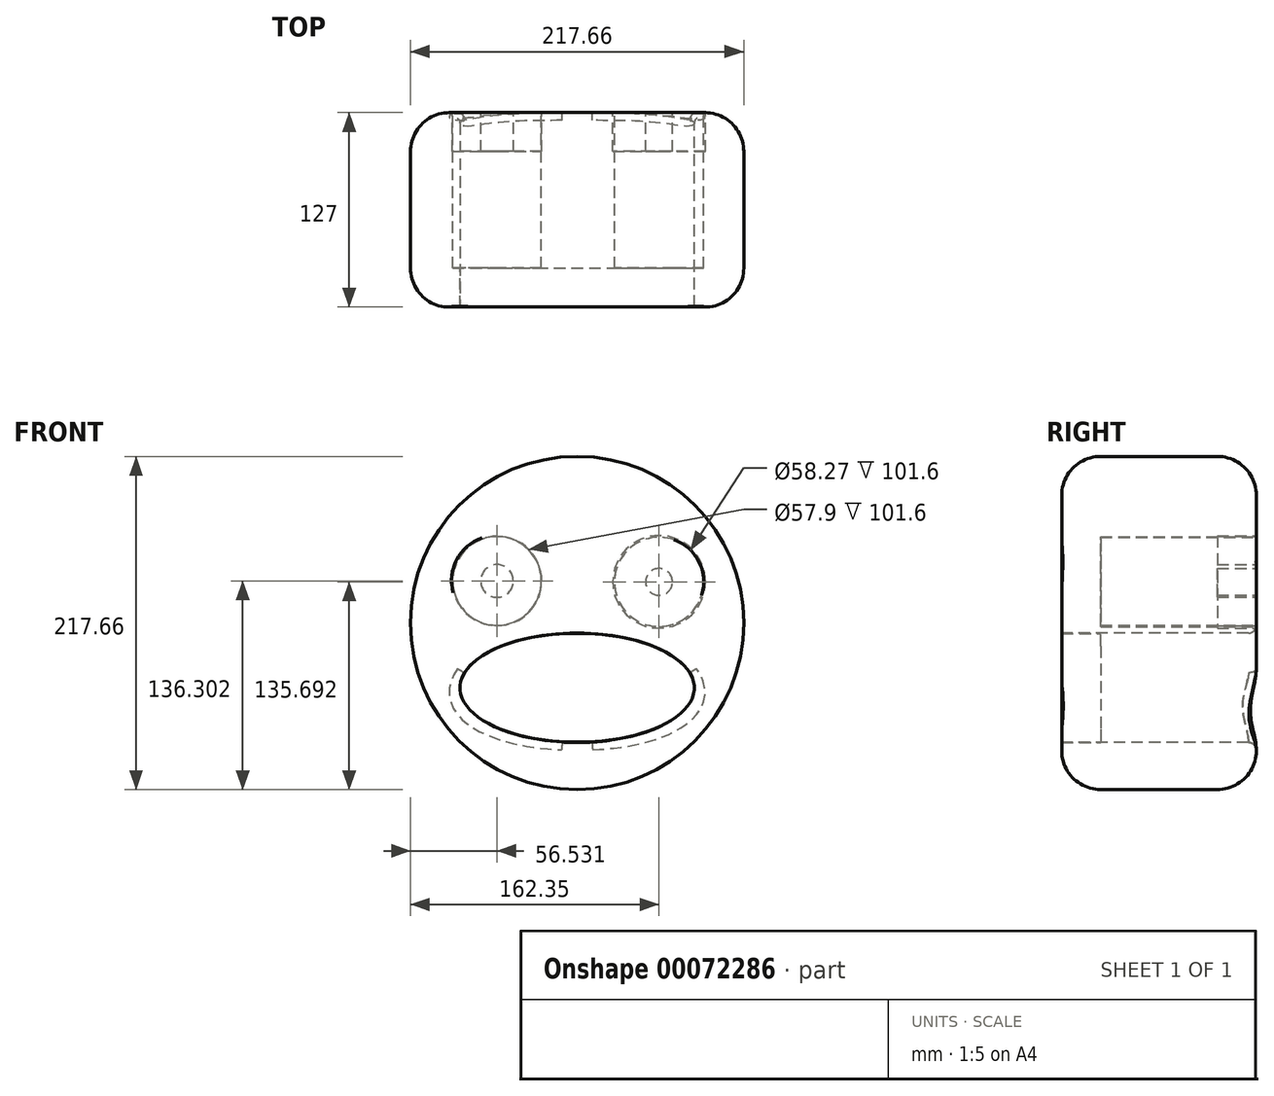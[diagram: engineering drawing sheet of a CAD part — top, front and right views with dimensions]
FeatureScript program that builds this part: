
annotation { "Feature Type Name" : "Feature", "Feature Type Description" : "" }
export const myFeature = defineFeature(function(context is Context, id is Id, definition is map)
    precondition{}
    {
        {
            var Q0;
            Q0=qCreatedBy(makeId("Front.planeOp"),FACE);
            var sketch = newSketch(context, id + "F0", { "sketchPlane" : qUnion([Q0])});
            skCircle(sketch, "E0", {"center": v(0, 0) * mm, "radius": 108.83 * mm});
            skCircle(sketch, "E1", {"center": v(-52.3, 27.47) * mm, "radius": 28.95 * mm});
            skCircle(sketch, "E2", {"center": v(53.52, 26.86) * mm, "radius": 29.14 * mm});
            skCircle(sketch, "E3", {"center": v(-52.3, 27.47) * mm, "radius": 10.65 * mm});
            skCircle(sketch, "E4", {"center": v(53.52, 26.86) * mm, "radius": 8.74 * mm});
            skEllipse(sketch, "E5", {"center": v(0, -42.33) * mm, "majorRadius": 76.51 * mm, "minorRadius": 35.71 * mm, "majorAxis": v(1, 0)});
            skSolve(sketch);
        }
        {
            var Q0;
            Q0 = qSketchRegion(id + "F0", true);
            extrude(context, id + "F1", {"entities" : qUnion([Q0]), "depth" : 127 * mm});
        }
        {
            var Q0;
            Q0=makeQuery(id+"F0.imprint","IMPRINT",FACE,{"disambiguationData":[TD([[makeQuery(id+"F0.imprint","IMPRINT",EDGE,{"derivedFrom":sQuery(id+"F0.wireOp",EDGE,"E4")}),1.0]])]});
            var Q1;
            Q1=makeQuery(id+"F0.imprint","IMPRINT",FACE,{"disambiguationData":[TD([[makeQuery(id+"F0.imprint","IMPRINT",EDGE,{"derivedFrom":sQuery(id+"F0.wireOp",EDGE,"E3")}),1.0]])]});
            extrude(context, id + "F2", {"entities" : qUnion([Q0, Q1]), "depth" : 25.4 * mm});
        }
        {
            var Q0;
            Q0=makeQuery(id+"F1.opExtrude","CAP_FACE",FACE,{"disambiguationData":[OSD([sQuery(id+"F0.wireOp",EDGE,"E0"),sQuery(id+"F0.wireOp",EDGE,"E1"),sQuery(id+"F0.wireOp",EDGE,"E2"),sQuery(id+"F0.wireOp",EDGE,"E5")])],"isStart":true});
            var sketch = newSketch(context, id + "F3", { "sketchPlane" : qUnion([Q0])});
            skCircle(sketch, "E6", {"center": v(-53.52, 26.86) * mm, "radius": 30.23 * mm});
            skCircle(sketch, "E7", {"center": v(52.3, 27.47) * mm, "radius": 29.21 * mm});
            skSolve(sketch);
        }
        {
            var Q0;
            Q0 = qSketchRegion(id + "F3", true);
            extrude(context, id + "F4", {"entities" : qUnion([Q0]), "oppositeDirection" : true, "depth" : 25.4 * mm});
        }
        {
            var Q0;
            Q0=makeQuery(id+"F1.opExtrude","CAP_FACE",FACE,{"disambiguationData":[OSD([sQuery(id+"F0.wireOp",EDGE,"E0"),sQuery(id+"F0.wireOp",EDGE,"E1"),sQuery(id+"F0.wireOp",EDGE,"E2"),sQuery(id+"F0.wireOp",EDGE,"E5")])],"isStart":false});
            var sketch = newSketch(context, id + "F5", { "sketchPlane" : qUnion([Q0])});
            skEllipse(sketch, "E8", {"center": v(0, -42.33) * mm, "majorRadius": 77.12 * mm, "minorRadius": 35.51 * mm, "majorAxis": v(1, 0)});
            skSolve(sketch);
        }
        {
            var Q0;
            {var subQ0=sQuery(id+"F5.wireOp",EDGE,"E8");var subQ1=makeQuery(id+"F1.opExtrude","CAP_EDGE",EDGE,{"disambiguationData":[OSD([sQuery(id+"F0.wireOp",EDGE,"E5")])],"isStart":false});var subQ2=makeQuery(id+"F5.imprint","INTERSECT",VERTEX,{"disambiguationData":[OD(0.0)],"derivedFrom":[subQ1,subQ0]});Q0=makeQuery(id+"F5.imprint","IMPRINT",FACE,{"disambiguationData":[TD([[makeQuery(id+"F5.imprint","IMPRINT",EDGE,{"disambiguationData":[TD([[subQ2,1.0]])],"derivedFrom":subQ0}),1.0]])]});}
            extrude(context, id + "F6", {"entities" : qUnion([Q0]), "oppositeDirection" : true, "depth" : 25.4 * mm});
        }
        {
            var Q0;
            Q0=makeQuery(id+"F1.opExtrude","CAP_EDGE",EDGE,{"disambiguationData":[OSD([sQuery(id+"F0.wireOp",EDGE,"E0")])],"isStart":true});
            var Q1;
            Q1=makeQuery(id+"F1.opExtrude","CAP_EDGE",EDGE,{"disambiguationData":[OSD([sQuery(id+"F0.wireOp",EDGE,"E0")])],"isStart":false});
            fillet(context, id + "F7", {"entities" : qUnion([Q0, Q1]), "radius" : 25.4 * mm, "tangentPropagation" : true, "allowEdgeOverflow" : false});
        }
        {
            var Q0;
            Q0=makeQuery(id+"F1.opExtrude","CAP_EDGE",EDGE,{"disambiguationData":[OSD([sQuery(id+"F0.wireOp",EDGE,"E5")])],"isStart":true});
            var Q1;
            Q1=makeQuery(id+"F7.opFillet","BLEND_EDGE",EDGE,{"disambiguationData":[OD(0.0)],"blendedFrom":[makeQuery(id+"F1.opExtrude","CAP_EDGE",EDGE,{"disambiguationData":[OSD([sQuery(id+"F0.wireOp",EDGE,"E0")])],"isStart":true}),makeQuery(id+"F1.opExtrude","SWEPT_FACE",FACE,{"disambiguationData":[OSD([sQuery(id+"F0.wireOp",EDGE,"E5")])]})],"blendedInto":[makeQuery(id+"F1.opExtrude","SWEPT_FACE",FACE,{"disambiguationData":[OSD([sQuery(id+"F0.wireOp",EDGE,"E5")])]})]});
            var Q2;
            Q2=makeQuery(id+"F7.opFillet","BLEND_EDGE",EDGE,{"disambiguationData":[OD(1.0)],"blendedFrom":[makeQuery(id+"F1.opExtrude","CAP_EDGE",EDGE,{"disambiguationData":[OSD([sQuery(id+"F0.wireOp",EDGE,"E0")])],"isStart":true}),makeQuery(id+"F1.opExtrude","SWEPT_FACE",FACE,{"disambiguationData":[OSD([sQuery(id+"F0.wireOp",EDGE,"E5")])]})],"blendedInto":[makeQuery(id+"F1.opExtrude","SWEPT_FACE",FACE,{"disambiguationData":[OSD([sQuery(id+"F0.wireOp",EDGE,"E5")])]})]});
            var Q3;
            Q3=makeQuery(id+"F1.opExtrude","CAP_EDGE",EDGE,{"disambiguationData":[OSD([sQuery(id+"F0.wireOp",EDGE,"E5")])],"isStart":true});
            fillet(context, id + "F8", {"entities" : qUnion([Q0, Q1, Q2, Q3]), "radius" : 5.08 * mm, "tangentPropagation" : true, "allowEdgeOverflow" : false});
        }
        {
            var Q0;
            Q0=makeQuery(id+"F7.opFillet","SPLIT",FACE,{"disambiguationData":[OD(1.0)],"derivedFrom":makeQuery(id+"F1.opExtrude","CAP_FACE",FACE,{"disambiguationData":[OSD([sQuery(id+"F0.wireOp",EDGE,"E0"),sQuery(id+"F0.wireOp",EDGE,"E1"),sQuery(id+"F0.wireOp",EDGE,"E2"),sQuery(id+"F0.wireOp",EDGE,"E5")])],"isStart":false})});
            var sketch = newSketch(context, id + "F9", { "sketchPlane" : qUnion([Q0])});
            skCircle(sketch, "E9", {"center": v(-52.3, 27.47) * mm, "radius": 29.77 * mm});
            skCircle(sketch, "E10", {"center": v(53.52, 26.86) * mm, "radius": 29.14 * mm});
            skSolve(sketch);
        }
        {
            var Q0;
            Q0 = qSketchRegion(id + "F9", true);
            extrude(context, id + "F10", {"entities" : qUnion([Q0]), "operationType" : NewBodyOperationType.ADD, "oppositeDirection" : true, "depth" : 25.4 * mm});
        }
    });
